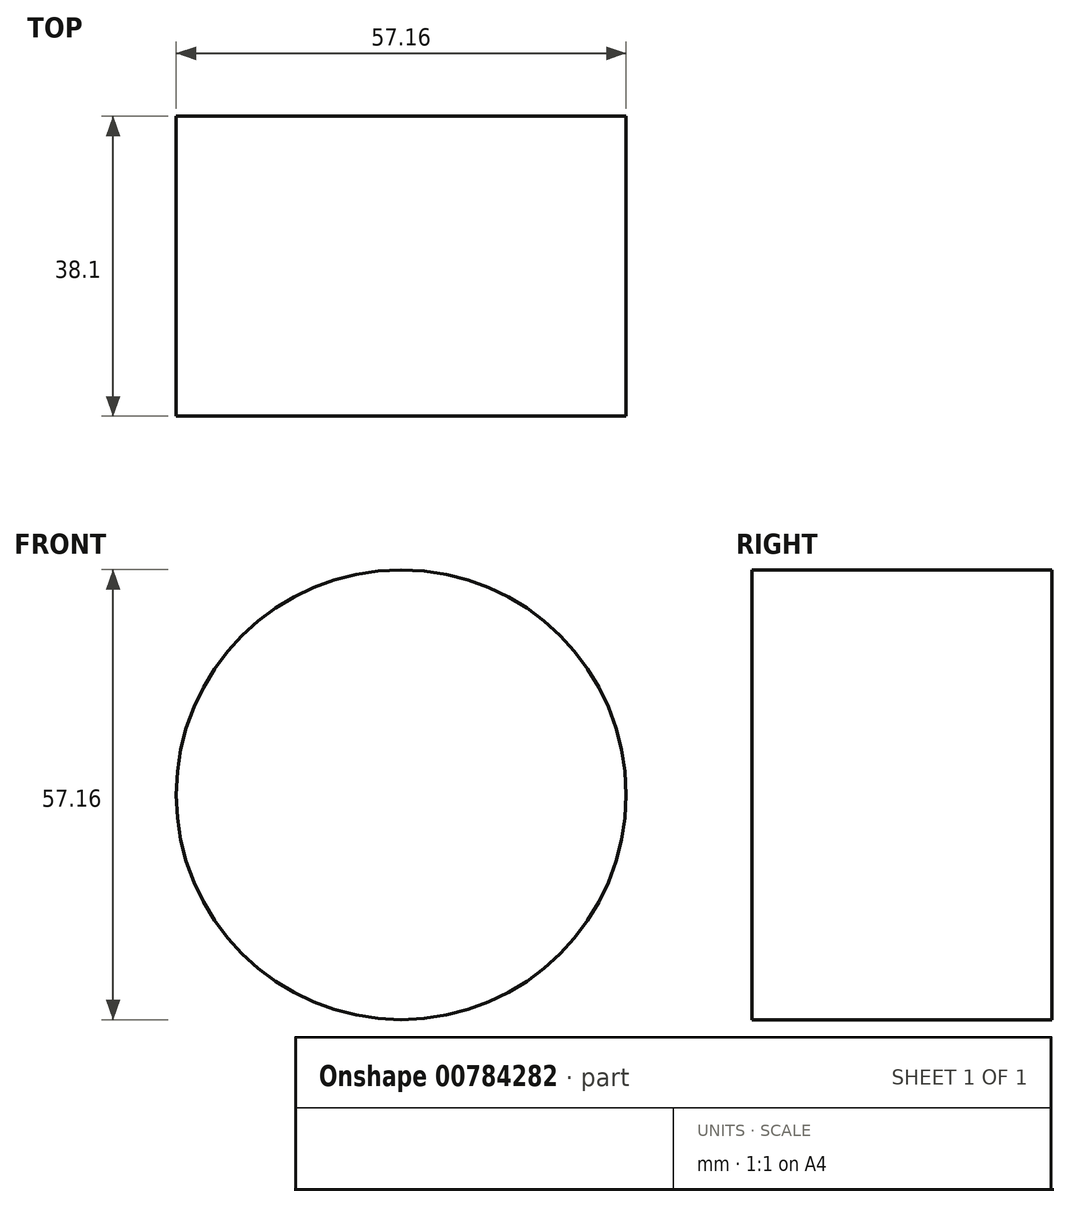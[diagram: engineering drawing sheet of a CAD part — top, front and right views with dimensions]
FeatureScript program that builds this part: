
annotation { "Feature Type Name" : "Feature", "Feature Type Description" : "" }
export const myFeature = defineFeature(function(context is Context, id is Id, definition is map)
    precondition{}
    {
        {
            var Q0;
            Q0=qCreatedBy(makeId("Front.planeOp"),FACE);
            var sketch = newSketch(context, id + "F0", { "sketchPlane" : qUnion([Q0])});
            skCircle(sketch, "E0", {"center": v(0, 0) * mm, "radius": 28.58 * mm});
            skSolve(sketch);
        }
        {
            var Q0;
            Q0 = qSketchRegion(id + "F0", true);
            extrude(context, id + "F1", {"entities" : qUnion([Q0]), "depth" : 38.1 * mm, "offsetDistance" : 25.4 * mm, "symmetric" : true});
        }
    });
